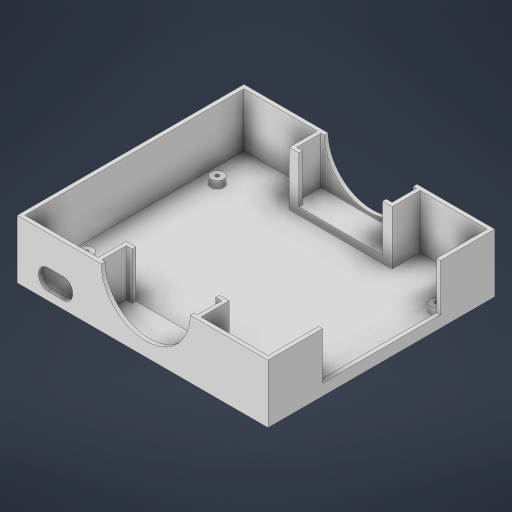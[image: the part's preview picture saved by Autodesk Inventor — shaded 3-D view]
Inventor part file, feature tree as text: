
AUTODESK INVENTOR PART (.ipt)
format: ipt  version: 2023 (Build 270158000, 158)  size: 408,064 bytes
history: native  units: in
note: dims shown in document units (in); Inventor stores cm internally (conversion verified against a paired STEP export)
features: sketch x13, extrude x12, reference x11, other x5, plane x3, projected_geometry x2, hole x1
ambient origin geometry x8: Origin, YZ Plane, XZ Plane, XY Plane, X Axis, Y Axis, Z Axis, Center Point
bodies: Solid1 (feature_tree)
feature tree (47):
  plane  "Work Plane1"
  extrude  "Extrusion1"  Depth=0.04in
  extrude  "Extrusion2"  Depth=0.5512in
  extrude  "Extrusion3"  Depth=0.065in
  extrude  "Extrusion4"  TaperAngle=0.0deg  [1 undecoded]
  extrude  "Extrusion5"  Depth=0.7874in TaperAngle=0.0deg
  extrude  "Extrusion6"  Depth=0.0787in TaperAngle=0.0deg
  sketch  "Sketch7"  dims[d16=0.05in d17=0.1181in d18=0.0in]
  plane  "Work Plane2"
  extrude  "Extrusion7"  Depth=0.1181in TaperAngle=0.0deg
  extrude  "Extrusion8"  Depth=0.1181in TaperAngle=0.0deg
  extrude  "Extrusion9"  Depth=0.1181in TaperAngle=0.0deg
  sketch  "Sketch10"  dims[d28=1.7853in d29=0.05in]
  plane  "Work Plane3"
  extrude  "Extrusion10"  Depth=0.05in
  extrude  "Extrusion11"  Depth=0.05in
  extrude  "Extrusion12"  Depth=0.8661in
  hole  "Hole1"  [1 undecoded]
  sketch  "Sketch1"  dims[d0=0.04in d1=0.04in]
  reference  "Reference1"
  reference  "Reference2"
  sketch  "Sketch2"  dims[d2=0.5512in d3=0.5512in]
  projected_geometry  "Projected Loop1"
  sketch  "Sketch3"  dims[d5=0.065in d6=0.065in]
  sketch  "Sketch4"  dims[d7=0.065in d8=0.0in]
  reference  "Reference3"
  reference  "Reference4"
  reference  "Reference5"
  reference  "Reference6"
  sketch  "Sketch5"  dims[d9=0.065in d10=0.7874in d11=0.0in]
  reference  "Reference7"
  reference  "Reference8"
  reference  "Reference9"
  sketch  "Sketch6"  dims[d12=0.1969in d13=0.0in d14=0.0787in d15=0.0in]
  reference  "Reference10"
  reference  "Reference11"
  sketch  "Sketch8"  dims[d19=0.6378in d22=0.1181in d23=0.0in]
  projected_geometry  "Projected Loop2"
  sketch  "Sketch9"  dims[d24=0.05in d25=0.1181in d26=0.0in]
  sketch  "Sketch11"  dims[d30=0.15in d31=0.05in]
  sketch  "Sketch12"  dims[d32=1.7323in d33=0.8661in]
  sketch  "Sketch13"  dims[d34=0.4724in d35=1.0in d36=0.0in d45=1.0in d46=0.0in d47=0.1in d48=0.1in d49=0.063in d50=0.063in d51=0.063in d52=0.063in d53=1.4961in d54=1.0in d55=0.0in d56=0.4724in d57=1.7323in d58=0.8661in d59=1.0in d60=0.0in d62=0.063in d63=0.1in d64=0.063in d65=0.063in d66=0.063in d67=0.1in d68=1.0in d69=0.0in d70=1.4961in d71=1.0in d72=0.0in d73=0.0617in d74=0.157in d75=0.173in d76=0.079in d77=0.5635in d78=1.0in d79=0.8108in]
  other  "<userpath>\Documents\Inventor\2024 Mavericks\Orange PI\OrangePICover.iam"
  other  "OrangePICover.iam"
  other  "OPi5_pcb_asm-0809:1"
  other  "orangepicover-002:1"
  other  "Assembly10"
note: 2 required parameter values undecoded (feature->parameter linkage not recoverable at this tier; creation-order binding heuristic only, values carry confidence <= 0.55)
